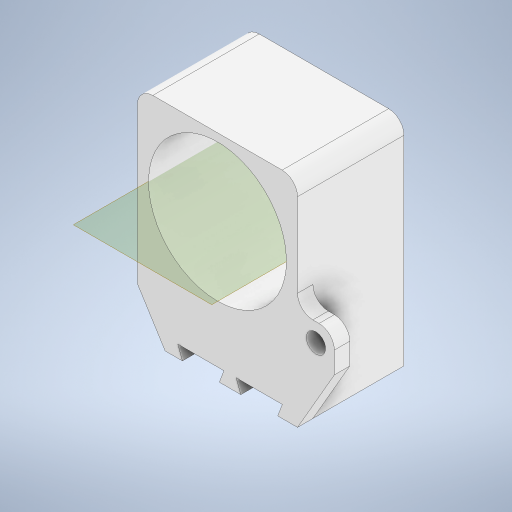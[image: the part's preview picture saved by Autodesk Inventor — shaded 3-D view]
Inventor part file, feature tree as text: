
AUTODESK INVENTOR PART (.ipt)
format: ipt  version: 2024 (Build 280153000, 153)  size: 586,240 bytes
history: native  units: in
note: dims shown in document units (in); Inventor stores cm internally (conversion verified against a paired STEP export)
features: reference x7, extrude x6, sketch x6, other x5, fillet x3, projected_geometry x3, plane x1, hole x1
ambient origin geometry x8: Origin, YZ Plane, XZ Plane, XY Plane, X Axis, Y Axis, Z Axis, Center Point
bodies: Solid1 (feature_tree)
feature tree (32):
  plane  "Work Plane1"
  extrude  "Extrusion1"  Depth=1.3024in TaperAngle=0.0deg
  extrude  "Extrusion2"  Depth=0.01in
  extrude  "Extrusion3"  Depth=0.375in
  extrude  "Extrusion4"  Depth=0.3in
  fillet  "Fillet1"  Radius=0.1in
  extrude  "Extrusion5"  Depth=0.125in TaperAngle=0.0deg
  sketch  "Sketch11"  dims[d22=0.125in d26=0.8in d27=0.5in d28=0.3438in d29=0.125in d30=0.125in d31=0.0in d32=0.0in d42=120.0deg d43=0.3in d45=0.3in d46=0.125in d47=0.15in d48=0.15in d49=0.125in d50=0.0in d51=0.125in d52=0.125in d54=0.1575in d55=0.75in d56=0.417in d57=0.118in d58=90.0deg d59=1.0in d60=0.0in d61=0.34in d62=0.475in d63=0.4554in]
  extrude  "Extrusion7"  Depth=0.125in
  fillet  "Fillet2"  Radius=0.5in
  fillet  "Fillet3"  Radius=0.3438in
  hole  "Hole2"  [1 undecoded]
  sketch  "Sketch1"  dims[d3=1.3024in d4=1.125in d5=0.0in]
  reference  "Reference1"
  reference  "Reference2"
  sketch  "Sketch5"  dims[d7=0.625in d8=0.0in d9=0.01in]
  reference  "Reference4"
  sketch  "Sketch6"  dims[d10=0.0in d11=0.0in d12=0.375in]
  projected_geometry  "Projected Loop1"
  sketch  "Sketch7"  dims[d13=0.3in d14=0.3in d15=0.1in]
  reference  "Reference5"
  reference  "Reference6"
  reference  "Reference7"
  reference  "Reference8"
  projected_geometry  "Projected Loop2"
  sketch  "Sketch8"  dims[d18=0.0in d19=0.0in d20=0.125in d21=0.0in]
  projected_geometry  "Projected Loop5"
  parser-record x1  (decoder bookkeeping rows leaked as tree rows — omitted from the tree; the rows remain in map.json)
  other  "Brushless Assembly.iam"
  other  "Brushless 2622 2600KV:1"
  other  "Brushless Motor Mount:1"
  other  "Assembly1"
note: 1 required parameter value undecoded (feature->parameter linkage not recoverable at this tier; creation-order binding heuristic only, values carry confidence <= 0.55)
note: 1 file-system path scrubbed to <path> (originals preserved in map.json)
